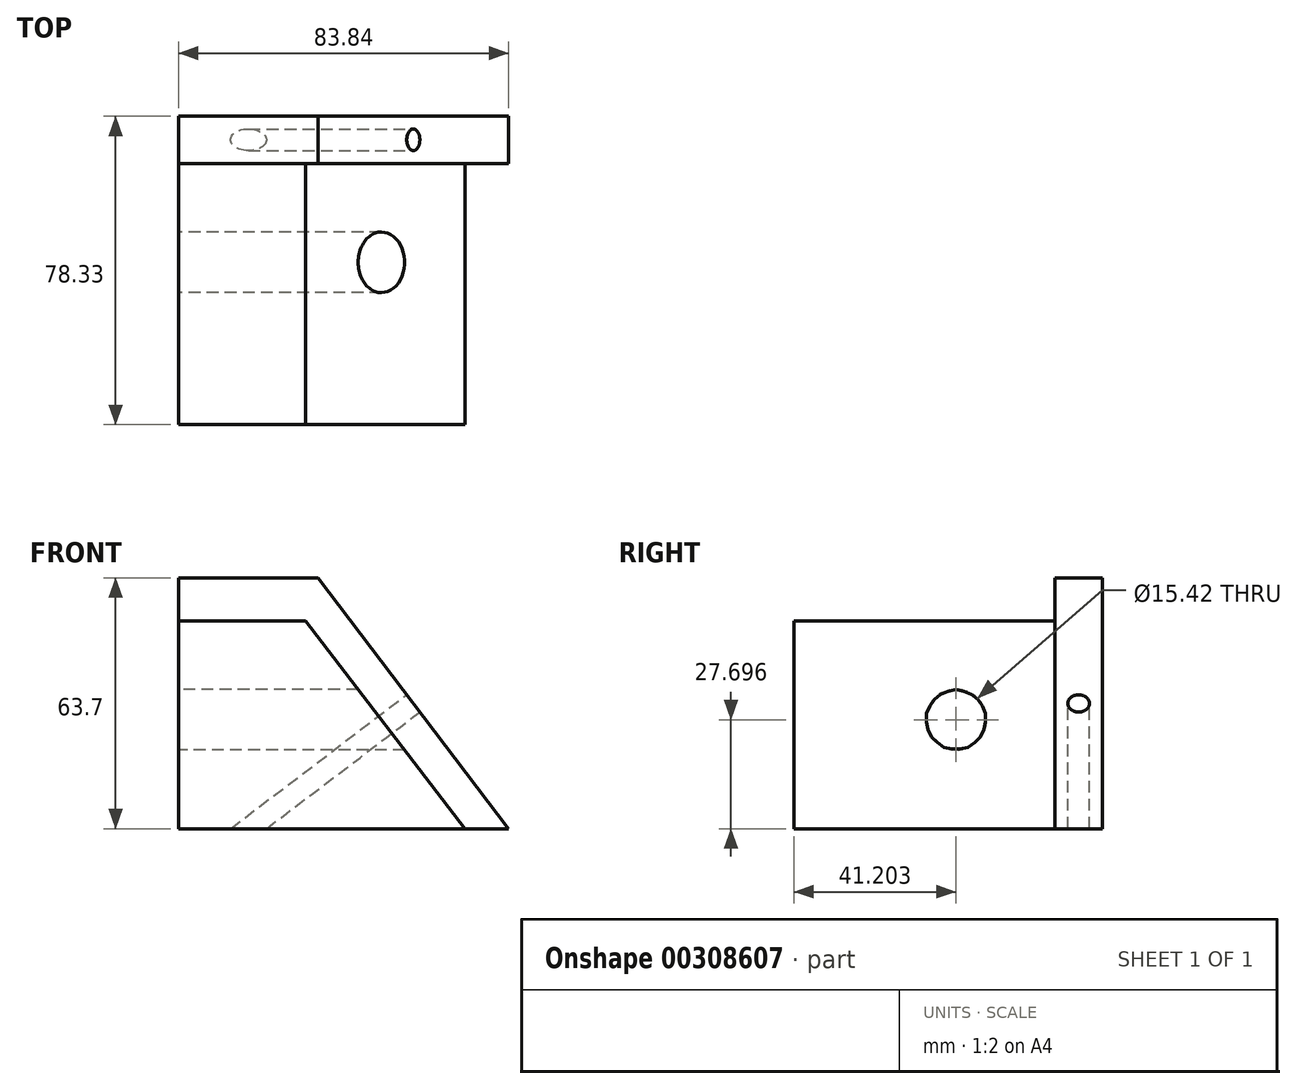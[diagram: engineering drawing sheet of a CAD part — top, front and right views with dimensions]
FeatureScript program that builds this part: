
annotation { "Feature Type Name" : "Feature", "Feature Type Description" : "" }
export const myFeature = defineFeature(function(context is Context, id is Id, definition is map)
    precondition{}
    {
        {
            var Q0;
            Q0=qCreatedBy(makeId("Front.planeOp"),FACE);
            var sketch = newSketch(context, id + "F0", { "sketchPlane" : qUnion([Q0])});
            skLineSegment(sketch, "E0", {"start": v(0, 0) * mm, "end": v(-72.8, 0) * mm});
            skLineSegment(sketch, "E1", {"start": v(-72.8, 0) * mm, "end": v(-72.8, 52.8) * mm});
            skLineSegment(sketch, "E2", {"start": v(-72.8, 52.8) * mm, "end": v(-40.57, 52.8) * mm});
            skLineSegment(sketch, "E3", {"start": v(-40.57, 52.8) * mm, "end": v(0, 0) * mm});
            skSolve(sketch);
        }
        {
            var Q0;
            Q0=makeQuery(id+"F0.imprint","IMPRINT",FACE,{"disambiguationData":[TD([[makeQuery(id+"F0.imprint","IMPRINT",EDGE,{"derivedFrom":sQuery(id+"F0.wireOp",EDGE,"E0")}),-1.0]])]});
            extrude(context, id + "F1", {"entities" : qUnion([Q0]), "depth" : 78.33 * mm});
        }
        {
            var Q0;
            Q0=makeQuery(id+"F1.opExtrude","SWEPT_FACE",FACE,{"disambiguationData":[OSD([sQuery(id+"F0.wireOp",EDGE,"E1")])]});
            var sketch = newSketch(context, id + "F2", { "sketchPlane" : qUnion([Q0])});
            skCircle(sketch, "E4", {"center": v(37.13, 27.7) * mm, "radius": 7.7 * mm});
            skSolve(sketch);
        }
        {
            var Q0;
            Q0=makeQuery(id+"F2.imprint","IMPRINT",FACE,{"disambiguationData":[TD([[makeQuery(id+"F2.imprint","IMPRINT",EDGE,{"derivedFrom":sQuery(id+"F2.wireOp",EDGE,"E4")}),1.0]])]});
            extrude(context, id + "F3", {"entities" : qUnion([Q0]), "operationType" : NewBodyOperationType.REMOVE, "oppositeDirection" : true, "depth" : 69 * mm});
        }
        {
            var Q0;
            Q0=makeQuery(id+"F1.opExtrude","CAP_FACE",FACE,{"disambiguationData":[OSD([sQuery(id+"F0.wireOp",EDGE,"E0"),sQuery(id+"F0.wireOp",EDGE,"E1"),sQuery(id+"F0.wireOp",EDGE,"E2"),sQuery(id+"F0.wireOp",EDGE,"E3")])],"isStart":true});
            var sketch = newSketch(context, id + "F4", { "sketchPlane" : qUnion([Q0])});
            skLineSegment(sketch, "E5", {"start": v(40.57, 52.8) * mm, "end": v(72.8, 52.8) * mm});
            skLineSegment(sketch, "E6", {"start": v(72.8, 52.8) * mm, "end": v(72.8, 63.7) * mm});
            skLineSegment(sketch, "E7", {"start": v(72.8, 63.7) * mm, "end": v(37.42, 63.7) * mm});
            skLineSegment(sketch, "E8", {"start": v(37.42, 63.7) * mm, "end": v(-11.03, 0) * mm});
            skLineSegment(sketch, "E9", {"start": v(-11.03, 0) * mm, "end": v(0, 0) * mm});
            skLineSegment(sketch, "E10", {"start": v(0, 0) * mm, "end": v(40.57, 52.8) * mm});
            skSolve(sketch);
        }
        {
            var Q0;
            Q0=makeQuery(id+"F4.imprint","IMPRINT",FACE,{"disambiguationData":[TD([[makeQuery(id+"F4.imprint","IMPRINT",EDGE,{"derivedFrom":sQuery(id+"F4.wireOp",EDGE,"E5")}),-1.0]])]});
            extrude(context, id + "F5", {"entities" : qUnion([Q0]), "operationType" : NewBodyOperationType.ADD, "oppositeDirection" : true, "depth" : 12 * mm});
        }
        {
            var Q0;
            Q0=makeQuery(id+"F5.opExtrude","SWEPT_FACE",FACE,{"disambiguationData":[OSD([sQuery(id+"F4.wireOp",EDGE,"E8")])]});
            var sketch = newSketch(context, id + "F6", { "sketchPlane" : qUnion([Q0])});
            skCircle(sketch, "E11", {"center": v(-6, 33.34) * mm, "radius": 2.76 * mm});
            skPoint(sketch, "E11.centerSnap0", {"position": v(-6, 73.35) * mm});
            skPoint(sketch, "E11.centerSnap1", {"position": v(-12, 33.34) * mm});
            skSolve(sketch);
        }
        {
            var Q0;
            Q0=makeQuery(id+"F6.imprint","IMPRINT",FACE,{"disambiguationData":[TD([[makeQuery(id+"F6.imprint","IMPRINT",EDGE,{"derivedFrom":sQuery(id+"F6.wireOp",EDGE,"E11")}),1.0]])]});
            extrude(context, id + "F7", {"entities" : qUnion([Q0]), "operationType" : NewBodyOperationType.REMOVE, "endBound" : BoundingType.THROUGH_ALL, "oppositeDirection" : true, "depth" : 25.4 * mm});
        }
    });
